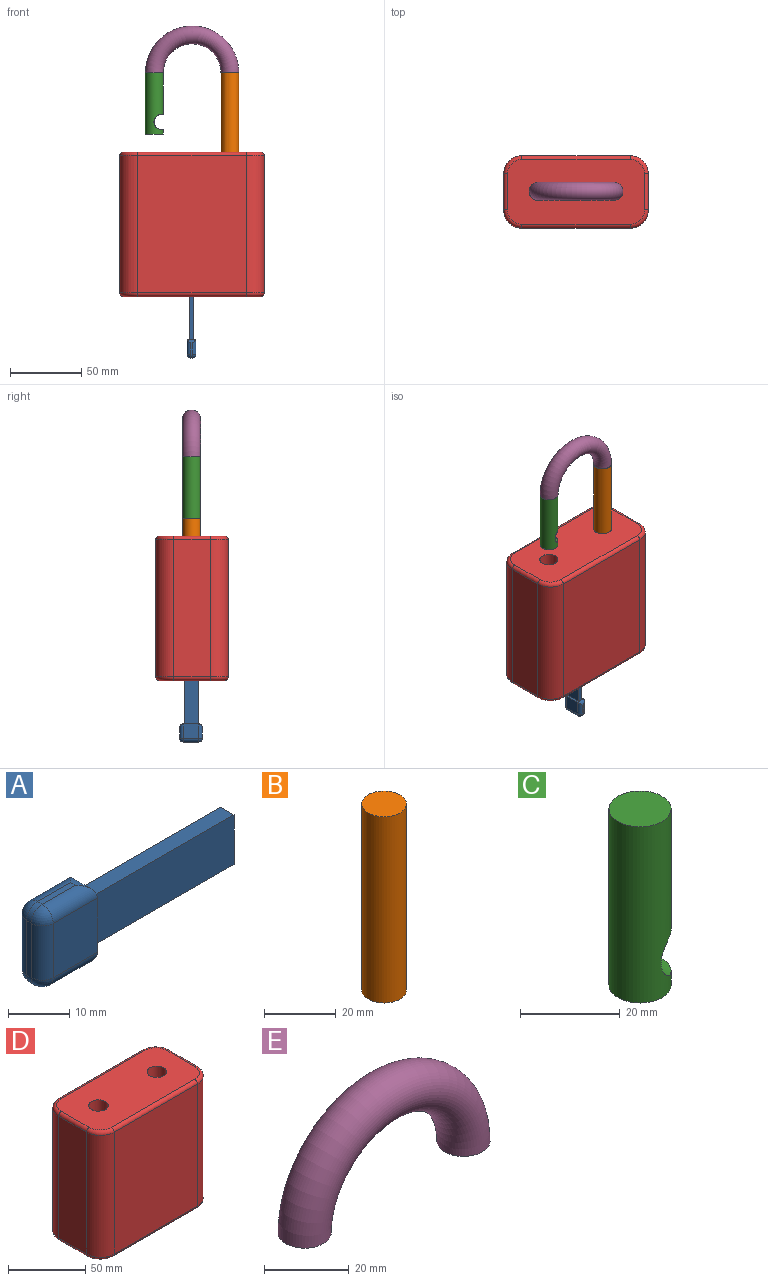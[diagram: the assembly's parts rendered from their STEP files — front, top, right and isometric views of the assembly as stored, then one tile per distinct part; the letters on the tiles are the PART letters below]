
ASSEMBLY  parts=5 mates=4
PART A: 25 faces, bbox 45.7x6.2x15.9 mm
  f0: plane 33.02x3.05mm, normal (0,0,-1), area 100.6mm2, adj f1,f3,f4,f5
  f1: plane 33.02x9.91mm, normal (0,1,0), area 327.1mm2, adj f0,f2,f4,f5
  f2: plane 33.02x3.05mm, normal (0,0,1), area 100.6mm2, adj f1,f3,f4,f5
  f3: plane 33.02x9.91mm, normal (0,-1,0), area 327.1mm2, adj f0,f2,f4,f5
  f4: plane 9.91x3.05mm, normal (1,0,0), area 30.2mm2, adj f0,f1,f2,f3
  f5: plane 10.84x6.16mm, normal (1,0,0), area 36.6mm2, adj f0,f1,f2,f3,f7,f9,f12,f23
  f6: plane 7.62x1.08mm, normal (0,0,1), area 8.2mm2, adj f19,f21,f23,f24
  f7: plane 10.84x10.16mm, normal (0,1,0), area 110.2mm2, adj f5,f15,f20,f24
  f8: plane 7.62x1.08mm, normal (0,0,-1), area 8.2mm2, adj f11,f12,f14,f15
  f9: plane 10.84x10.16mm, normal (0,-1,0), area 110.2mm2, adj f5,f11,f16,f21
  f10: plane 10.84x1.08mm, normal (-1,0,0), area 11.7mm2, adj f14,f16,f19,f20
  f11: cylinder r=2.54mm len=10.16mm, axis (-1,0,0), area 36.9mm2, adj f8,f9,f12,f13
  f12: cylinder r=2.54mm len=6.16mm, axis (0,-1,0), area 17.2mm2, adj f5,f8,f11,f15
  f13: sphere r=2.54mm, area 10.1mm2, adj f11,f14,f16
  f14: cylinder r=2.54mm len=2.54mm, axis (0,1,0), area 4.3mm2, adj f8,f10,f13,f17
  f15: cylinder r=2.54mm len=10.16mm, axis (1,0,0), area 36.9mm2, adj f7,f8,f12,f17
  f16: cylinder r=2.54mm len=10.84mm, axis (0,0,-1), area 43.3mm2, adj f9,f10,f13,f18
  f17: sphere r=2.54mm, area 10.1mm2, adj f14,f15,f20
  f18: sphere r=2.54mm, area 10.1mm2, adj f16,f19,f21
  f19: cylinder r=2.54mm len=2.54mm, axis (0,-1,0), area 4.3mm2, adj f6,f10,f18,f22
  f20: cylinder r=2.54mm len=10.84mm, axis (0,0,1), area 43.3mm2, adj f7,f10,f17,f22
  f21: cylinder r=2.54mm len=10.16mm, axis (1,0,0), area 36.9mm2, adj f6,f9,f18,f23
  f22: sphere r=2.54mm, area 10.1mm2, adj f19,f20,f24
  f23: cylinder r=2.54mm len=6.16mm, axis (0,1,0), area 17.2mm2, adj f5,f6,f21,f24
  f24: cylinder r=2.54mm len=10.16mm, axis (-1,0,0), area 36.9mm2, adj f6,f7,f22,f23
PART B: 3 faces, bbox 12.4x12.4x63.5 mm
  f0: plane 12.45x12.45mm, normal (0,0,1), area 121.7mm2, adj f1
  f1: cylinder r=6.22mm len=63.5mm, axis (0,0,1), area 2482.9mm2, adj f0,f2
  f2: plane 12.45x12.45mm, normal (0,0,-1), area 121.7mm2, adj f1
PART C: 4 faces, bbox 12.4x12.4x43.2 mm
  f0: plane 12.45x12.45mm, normal (0,0,1), area 121.7mm2, adj f2
  f1: plane 12.45x12.45mm, normal (0,0,-1), area 121.7mm2, adj f2
  f2: cylinder r=6.22mm len=43.18mm, axis (0,0,1), area 1502.4mm2, adj f0,f1,f3
  f3: cylinder r=5.27mm len=12.45mm, axis (0,-1,0), area 202.1mm2, adj f2
PART D: 37 faces, bbox 103.7x52.9x101.6 mm
  f0: plane 17.78x17.78mm, normal (0,0,-1), area 216mm2, adj f15,f16,f17,f18,f19
  f1: plane 96.52x45.72mm, normal (0,0,1), area 4070.9mm2, adj f11,f13,f29,f30,f31,f32,f33,f34
  f2: plane 96.52x25.4mm, normal (-1,0,0), area 2451.6mm2, adj f3,f9,f23,f31
  f3: cylinder r=12.7mm len=96.52mm, axis (0,0,-1), area 1925.5mm2, adj f2,f4,f21,f29
  f4: plane 96.52x76.2mm, normal (0,-1,0), area 7354.8mm2, adj f3,f5,f22,f30
  f5: cylinder r=12.7mm len=96.52mm, axis (0,0,-1), area 1925.5mm2, adj f4,f6,f24,f32
  f6: plane 96.52x25.4mm, normal (1,0,0), area 2451.6mm2, adj f5,f7,f26,f34
  f7: cylinder r=12.7mm len=96.52mm, axis (0,0,-1), area 1925.5mm2, adj f6,f8,f28,f36
  f8: plane 96.52x76.2mm, normal (0,1,0), area 7354.8mm2, adj f7,f9,f27,f35
  f9: cylinder r=12.7mm len=96.52mm, axis (0,0,-1), area 1925.5mm2, adj f2,f8,f25,f33
  f10: plane 96.52x45.72mm, normal (0,0,-1), area 3913.9mm2, adj f15,f21,f22,f23,f24,f25,f26,f27
  f11: cylinder r=6.35mm len=38.1mm, axis (0,0,1), area 1520.1mm2, adj f1,f12
  f12: plane 12.7x12.7mm, normal (0,0,1), area 126.7mm2, adj f11
  f13: cylinder r=6.35mm len=38.1mm, axis (0,0,1), area 1520.1mm2, adj f1,f14
  f14: plane 12.7x12.7mm, normal (0,0,1), area 126.7mm2, adj f13
  f15: torus R=11.43mm, axis (0,0,1), area 246mm2, adj f0,f10
  f16: plane 25.4x10.16mm, normal (1,0,0), area 258.1mm2, adj f0,f17,f19,f20
  f17: plane 25.4x3.18mm, normal (0,-1,0), area 80.6mm2, adj f0,f16,f18,f20
  f18: plane 25.4x10.16mm, normal (-1,0,0), area 258.1mm2, adj f0,f17,f19,f20
  f19: plane 25.4x3.18mm, normal (0,1,0), area 80.6mm2, adj f0,f16,f18,f20
  f20: plane 10.16x3.18mm, normal (0,0,-1), area 32.3mm2, adj f16,f17,f18,f19
  f21: torus R=10.16mm, axis (0,0,1), area 73.8mm2, adj f3,f10,f22,f23
  f22: cylinder r=2.54mm len=76.2mm, axis (1,0,0), area 304mm2, adj f4,f10,f21,f24
  f23: cylinder r=2.54mm len=25.4mm, axis (0,-1,0), area 101.3mm2, adj f2,f10,f21,f25
  f24: torus R=10.16mm, axis (0,0,1), area 73.8mm2, adj f5,f10,f22,f26
  f25: torus R=10.16mm, axis (0,0,1), area 73.8mm2, adj f9,f10,f23,f27
  f26: cylinder r=2.54mm len=25.4mm, axis (0,1,0), area 101.3mm2, adj f6,f10,f24,f28
  f27: cylinder r=2.54mm len=76.2mm, axis (-1,0,0), area 304mm2, adj f8,f10,f25,f28
  f28: torus R=10.16mm, axis (0,0,1), area 73.8mm2, adj f7,f10,f26,f27
  f29: torus R=10.16mm, axis (0,0,1), area 73.8mm2, adj f1,f3,f30,f31
  f30: cylinder r=2.54mm len=76.2mm, axis (-1,0,0), area 304mm2, adj f1,f4,f29,f32
  f31: cylinder r=2.54mm len=25.4mm, axis (0,1,0), area 101.3mm2, adj f1,f2,f29,f33
  f32: torus R=10.16mm, axis (0,0,1), area 73.8mm2, adj f1,f5,f30,f34
  f33: torus R=10.16mm, axis (0,0,1), area 73.8mm2, adj f1,f9,f31,f35
  f34: cylinder r=2.54mm len=25.4mm, axis (0,-1,0), area 101.3mm2, adj f1,f6,f32,f36
  f35: cylinder r=2.54mm len=76.2mm, axis (1,0,0), area 304mm2, adj f1,f8,f33,f36
  f36: torus R=10.16mm, axis (0,0,1), area 73.8mm2, adj f1,f7,f34,f35
PART E: 3 faces, bbox 71.2x12.6x35.6 mm
  f0: plane 12.57x12.57mm, normal (0,0,-1), area 124.2mm2, adj f2
  f1: plane 12.57x12.57mm, normal (0,0,-1), area 124.2mm2, adj f2
  f2: torus R=26.58mm, axis (0,1,0), area 3298.8mm2, adj f0,f1
PLACE A rot(axis=(-0.58,-0.58,-0.58),120deg) t=(-12.94,9.41,-223.11)mm
PLACE B rot(axis=(0,0,1),0deg) t=(-14.07,14.14,-98.65)mm
PLACE C rot(axis=(0,0,1),0deg) t=(-14.15,14.14,-98.65)mm
PLACE D rot(axis=(0,0,1),0deg) t=(-14.13,14.14,-192.63)mm fixed
PLACE E rot(axis=(0,0,1),0deg) t=(-0.07,14.14,-35.15)mm
MATE fastened E.f0 <-> C.f2  axis (0,0,-1) through (-40.63,14.14,-35.15)mm
MATE fastened E.f1 <-> B.f1  axis (0,0,-1) through (12.54,14.14,-35.15)mm
MATE slider D.f13 <-> B.f1  axis (0,0,1) through (12.54,14.14,-91.03)mm
MATE slider A.f4 <-> D.f15  axis (0,0,1) through (-14.47,14.36,-190.09)mm
